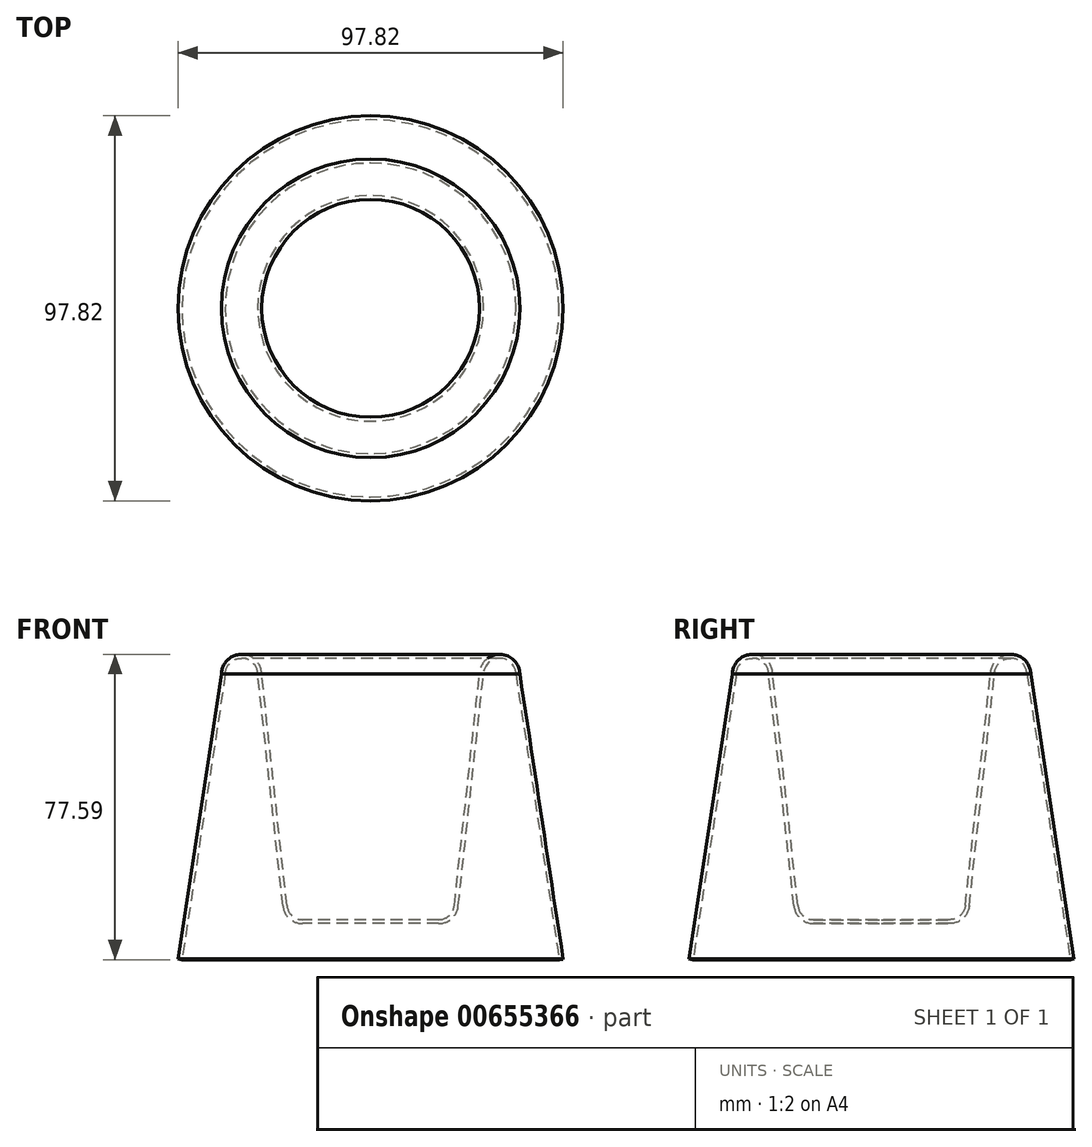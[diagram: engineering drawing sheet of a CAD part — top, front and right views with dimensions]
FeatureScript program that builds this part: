
annotation { "Feature Type Name" : "Feature", "Feature Type Description" : "" }
export const myFeature = defineFeature(function(context is Context, id is Id, definition is map)
    precondition{}
    {
        {
            var Q0;
            Q0=qCreatedBy(makeId("Front.planeOp"),FACE);
            var sketch = newSketch(context, id + "F0", { "sketchPlane" : qUnion([Q0])});
            skLineSegment(sketch, "E0", {"start": v(0, -27.75) * mm, "end": v(-17.3, -27.75) * mm});
            skLineSegment(sketch, "E1", {"start": v(-22.27, -23.29) * mm, "end": v(-28.66, 35.54) * mm});
            skLineSegment(sketch, "E2", {"start": v(-36.92, 35.54) * mm, "end": v(-47.92, -36.92) * mm});
            skArc(sketch, "E3", {"start": v(-28.66, 35.54) * mm, "mid": v(-32.79, 39.67) * mm, "end": v(-36.92, 35.54) * mm});
            skPoint(sketch, "E4.visualSharp", {"position": v(-21.78, -27.75) * mm});
            skArc(sketch, "E4.filletArc", {"start": v(-22.27, -23.29) * mm, "mid": v(-20.64, -26.47) * mm, "end": v(-17.3, -27.75) * mm});
            skLineSegment(sketch, "E5.0", {"start": v(-37.92, 35.62) * mm, "end": v(-48.91, -36.77) * mm});
            skLineSegment(sketch, "E5.1", {"start": v(0, -26.75) * mm, "end": v(-17.3, -26.75) * mm});
            skArc(sketch, "E5.2", {"start": v(-21.27, -23.18) * mm, "mid": v(-19.97, -25.72) * mm, "end": v(-17.3, -26.75) * mm});
            skLineSegment(sketch, "E5.3", {"start": v(-21.27, -23.18) * mm, "end": v(-27.66, 35.6) * mm});
            skArc(sketch, "E5.4", {"start": v(-27.66, 35.6) * mm, "mid": v(-32.78, 40.67) * mm, "end": v(-37.92, 35.62) * mm});
            skLineSegment(sketch, "E6", {"start": v(0, -26.75) * mm, "end": v(0, -27.75) * mm});
            skPoint(sketch, "E7.orphan", {"position": v(-46.56, -36.92) * mm});
            skLineSegment(sketch, "E8", {"start": v(-48.91, -36.77) * mm, "end": v(-47.92, -36.92) * mm});
            skSolve(sketch);
        }
        {
            var Q0;
            Q0 = qSketchRegion(id + "F0", true);
            var Q1;
            Q1=sQuery(id+"F0.wireOp",EDGE,"E6");
            revolve(context, id + "F1", {"entities" : qUnion([Q0]), "axis" : qUnion([Q1]), "revolveType" : RevolveType.FULL});
        }
    });
